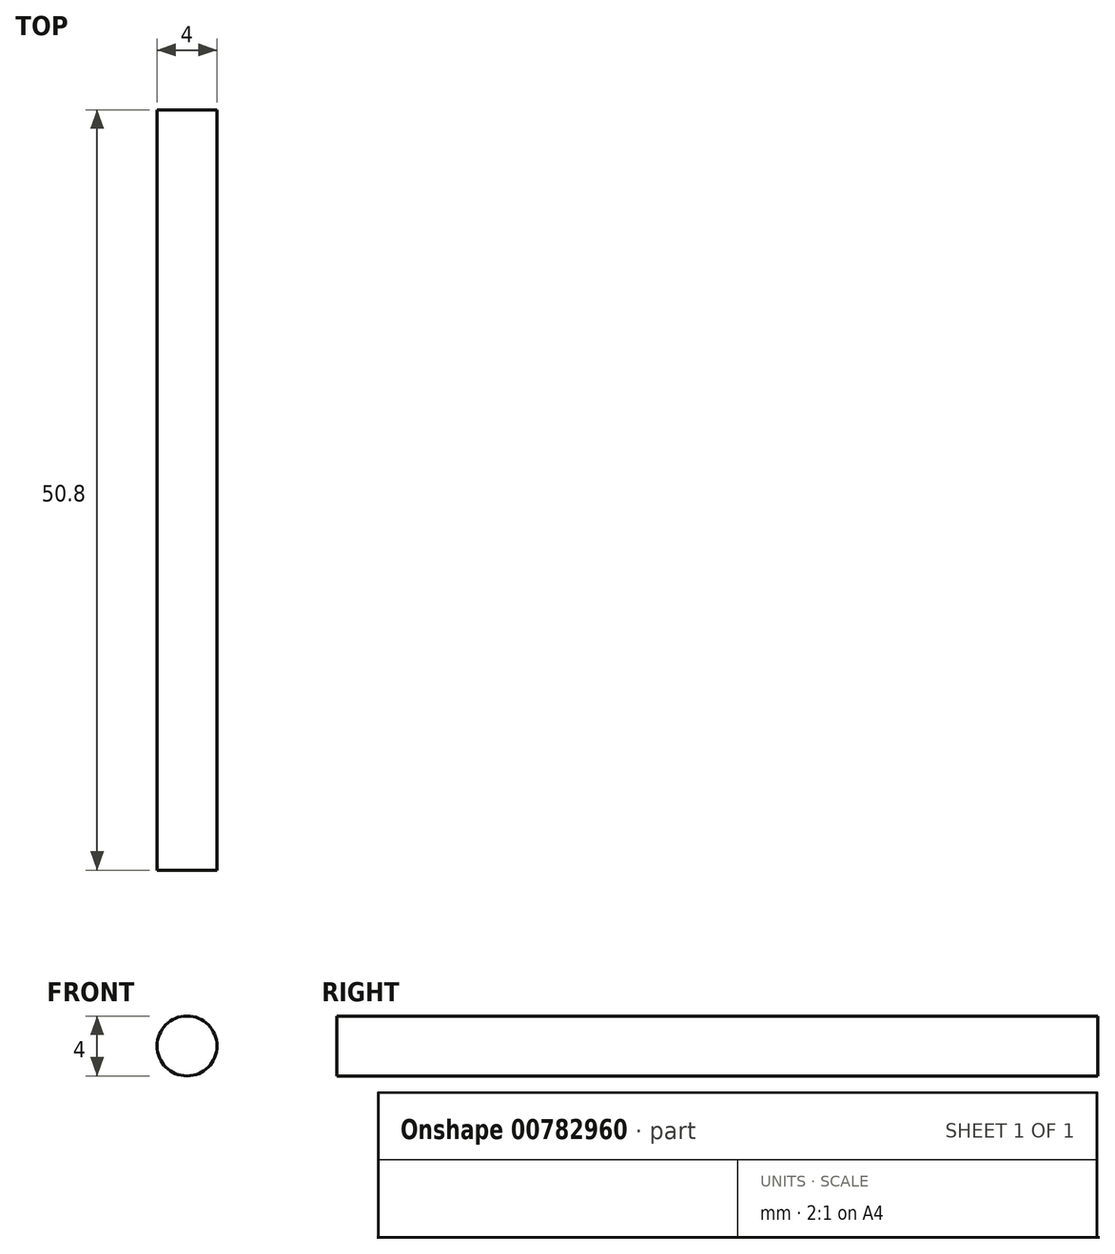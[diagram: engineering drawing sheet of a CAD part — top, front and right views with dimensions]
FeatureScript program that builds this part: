
annotation { "Feature Type Name" : "Feature", "Feature Type Description" : "" }
export const myFeature = defineFeature(function(context is Context, id is Id, definition is map)
    precondition{}
    {
        {
            var Q0;
            Q0=qCreatedBy(makeId("Front.planeOp"),FACE);
            var sketch = newSketch(context, id + "F0", { "sketchPlane" : qUnion([Q0])});
            skCircle(sketch, "E0", {"center": v(0, 0) * mm, "radius": 2 * mm});
            skSolve(sketch);
        }
        {
            var Q0;
            Q0=qSketchRegion(id+"F0",true);
            extrude(context, id + "F1", {"entities" : qUnion([Q0]), "depth" : 50.8 * mm, "offsetDistance" : 25 * mm});
        }
    });
